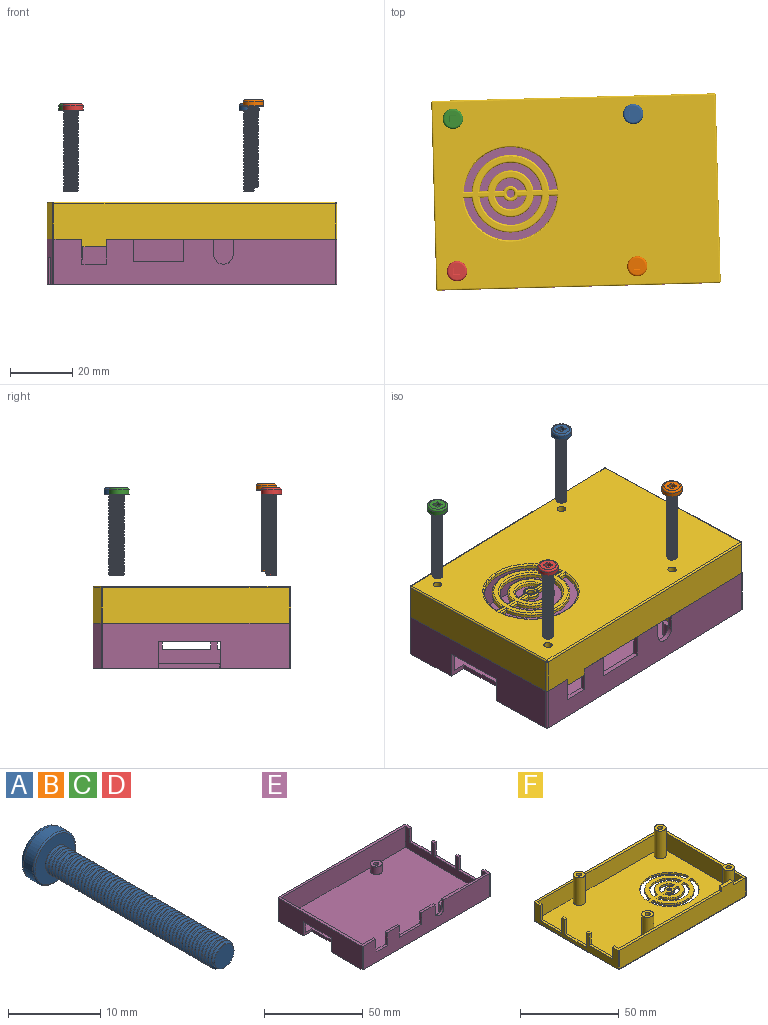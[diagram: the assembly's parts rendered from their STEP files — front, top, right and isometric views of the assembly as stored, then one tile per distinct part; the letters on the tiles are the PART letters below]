
ASSEMBLY  parts=6 mates=5
PART A: 21 faces, bbox 7.2x28.3x7.2 mm
  f0: plane 5.24x5.24mm, normal (0,1,0), area 16.8mm2, adj f4,f17,f18,f19,f20
  f1: plane 6.29x6.29mm, normal (0,-1,0), area 22mm2, adj f2,f5,f9,f10,f11
  f2: cylinder r=1.5mm len=26mm, axis (0,1,0), area 291.6mm2, adj f1,f6,f8,f9,f10,f11
  f3: cylinder r=3.25mm len=6.5mm, axis (0,1,0), area 28.7mm2, adj f4,f5
  f4: torus R=2.62mm, axis (0,-1,0), area 18.7mm2, adj f0,f3
  f5: torus R=3.08mm, axis (0,-1,0), area 5.3mm2, adj f1,f3
  f6: plane 3x3mm, normal (0,-1,0), area 7.1mm2, adj f2,f7
  f7: cylinder r=1.5mm len=0.03mm, axis (0,1,0), area 0mm2, adj f6,f8,f11
  f8: plane 0.3x0.26mm, normal (0,0,-1), area 0mm2, adj f2,f7,f10,f11
  f9: plane 0x0mm, normal (0,0,1), area 0mm2, adj f1,f2,f11
  f10: bspline ~26.07x4.07mm, area 159.4mm2, adj f1,f2,f8,f11
  f11: bspline ~26.15x4.07mm, area 158.7mm2, adj f1,f2,f7,f8,f9,f10
  f12: plane 2x1.1mm, normal (0,0,1), area 2.2mm2, adj f13,f15,f16,f17
  f13: plane 2x1.1mm, normal (1,0,0), area 2.2mm2, adj f12,f14,f16,f18
  f14: plane 2x1.1mm, normal (0,0,-1), area 2.2mm2, adj f13,f15,f16,f20
  f15: plane 2x1.1mm, normal (-1,0,0), area 2.2mm2, adj f12,f14,f16,f19
  f16: plane 2x2mm, normal (0,1,0), area 4mm2, adj f12,f13,f14,f15
  f17: cylinder r=0.1mm len=2.2mm, axis (-1,0,0), area 0.3mm2, adj f0,f12,f18,f19
  f18: cylinder r=0.1mm len=2.2mm, axis (0,0,1), area 0.3mm2, adj f0,f13,f17,f20
  f19: cylinder r=0.1mm len=2.2mm, axis (0,0,-1), area 0.3mm2, adj f0,f15,f17,f20
  f20: cylinder r=0.1mm len=2.2mm, axis (1,0,0), area 0.3mm2, adj f0,f14,f18,f19
PART B: same geometry as A
PART C: same geometry as A
PART D: same geometry as A
PART E: 58 faces, bbox 91.5x61x14.5 mm
  f0: plane 2x1.5mm, normal (0,0,1), area 3mm2, adj f3,f4,f33,f35
  f1: plane 2x1.5mm, normal (0,0,1), area 3mm2, adj f3,f4,f29,f32
  f2: plane 91.5x61mm, normal (0,0,1), area 243mm2, adj f3,f4,f5,f7,f11,f12,f13,f15
  f3: plane 60x14.5mm, normal (1,0,0), area 473.3mm2, adj f0,f1,f2,f10,f14,f29,f30,f31
  f4: plane 58x13mm, normal (-1,0,0), area 357.3mm2, adj f0,f1,f2,f6,f10,f11,f15,f29
  f5: plane 58x13mm, normal (1,0,0), area 611.4mm2, adj f2,f6,f11,f15,f25,f26,f27
  f6: plane 88.5x58mm, normal (0,0,1), area 4934.8mm2, adj f4,f5,f11,f15,f25,f26,f28,f39
  f7: plane 90.5x14.5mm, normal (0,-1,0), area 1086.9mm2, adj f2,f8,f9,f10,f14,f16,f17,f18
  f8: plane 8.7x1.5mm, normal (0,0,1), area 13mm2, adj f7,f11,f19,f24
  f9: plane 9.7x1.5mm, normal (0,0,1), area 14.5mm2, adj f7,f11,f18,f21
  f10: plane 33.3x4.6mm, normal (0,0,1), area 54.5mm2, adj f3,f4,f7,f11,f17,f36,f55
  f11: plane 88.5x13mm, normal (0,1,0), area 925.2mm2, adj f2,f4,f5,f6,f8,f9,f10,f16
  f12: plane 60x14.5mm, normal (-1,0,0), area 697.7mm2, adj f2,f14,f25,f26,f27,f54,f57
  f13: plane 90.5x14.5mm, normal (0,1,0), area 1312.3mm2, adj f2,f14,f56,f57
  f14: plane 91.5x61mm, normal (0,0,-1), area 5466.4mm2, adj f3,f7,f12,f13,f25,f26,f28,f54
  f15: plane 88.5x13mm, normal (0,-1,0), area 1150.5mm2, adj f2,f4,f5,f6
  f16: cylinder r=3.15mm len=6.3mm, axis (0,-1,0), area 14.8mm2, adj f7,f11,f17,f18
  f17: plane 4.85x1.5mm, normal (-1,0,0), area 7.3mm2, adj f7,f10,f11,f16
  f18: plane 4.85x1.5mm, normal (1,0,0), area 7.3mm2, adj f7,f9,f11,f16
  f19: plane 7.2x1.5mm, normal (1,0,0), area 10.8mm2, adj f7,f8,f11,f20
  f20: plane 16x1.5mm, normal (0,0,1), area 24mm2, adj f7,f11,f19,f21
  f21: plane 7.2x1.5mm, normal (-1,0,0), area 10.8mm2, adj f7,f9,f11,f20
  f22: plane 8x1.5mm, normal (1,0,0), area 12mm2, adj f2,f7,f11,f23
  f23: plane 8x1.5mm, normal (0,0,1), area 12mm2, adj f7,f11,f22,f24
  f24: plane 8x1.5mm, normal (-1,0,0), area 12mm2, adj f7,f8,f11,f23
  f25: plane 8.7x5.8mm, normal (0,-1,0), area 19.5mm2, adj f5,f6,f12,f14,f27,f28
  f26: plane 8.7x5.8mm, normal (0,1,0), area 19.5mm2, adj f5,f6,f12,f14,f27,f28
  f27: plane 19.8x1.5mm, normal (0,0,-1), area 29.7mm2, adj f5,f12,f25,f26
  f28: plane 19.8x1.5mm, normal (-1,0,0), area 29.7mm2, adj f6,f14,f25,f26
  f29: plane 8.3x1.5mm, normal (0,1,0), area 12.5mm2, adj f1,f3,f4,f30
  f30: plane 15.6x1.5mm, normal (0,0,1), area 23.4mm2, adj f3,f4,f29,f31
  f31: plane 8.3x1.5mm, normal (0,-1,0), area 12.5mm2, adj f2,f3,f4,f30
  f32: plane 8.3x1.5mm, normal (0,-1,0), area 12.5mm2, adj f1,f3,f4,f34
  f33: plane 8.3x1.5mm, normal (0,1,0), area 12.5mm2, adj f0,f3,f4,f34
  f34: plane 15.6x1.5mm, normal (0,0,1), area 23.4mm2, adj f3,f4,f32,f33
  f35: plane 8.3x1.5mm, normal (0,-1,0), area 12.5mm2, adj f0,f3,f4,f37
  f36: plane 8.3x1.5mm, normal (0,1,0), area 12.5mm2, adj f3,f4,f10,f37
  f37: plane 16.6x1.5mm, normal (0,0,1), area 24.9mm2, adj f3,f4,f35,f36
  f38: cylinder r=1.32mm len=4.7mm, axis (0,0,-1), area 39.1mm2, adj f40,f41
  f39: cylinder r=3mm len=6mm, axis (0,0,-1), area 88.6mm2, adj f6,f40
  f40: plane 6x6mm, normal (0,0,1), area 22.8mm2, adj f38,f39
  f41: plane 2.65x2.65mm, normal (0,0,1), area 5.5mm2, adj f38
  f42: cylinder r=1.32mm len=4.7mm, axis (0,0,-1), area 39.1mm2, adj f44,f45
  f43: cylinder r=3mm len=6mm, axis (0,0,-1), area 88.6mm2, adj f6,f44
  f44: plane 6x6mm, normal (0,0,1), area 22.8mm2, adj f42,f43
  f45: plane 2.65x2.65mm, normal (0,0,1), area 5.5mm2, adj f42
  f46: cylinder r=1.32mm len=4.7mm, axis (0,0,-1), area 39.1mm2, adj f48,f49
  f47: cylinder r=3mm len=6mm, axis (0,0,-1), area 88.6mm2, adj f6,f48
  f48: plane 6x6mm, normal (0,0,1), area 22.8mm2, adj f46,f47
  f49: plane 2.65x2.65mm, normal (0,0,1), area 5.5mm2, adj f46
  f50: cylinder r=1.32mm len=4.7mm, axis (0,0,-1), area 39.1mm2, adj f52,f53
  f51: cylinder r=3mm len=6mm, axis (0,0,-1), area 88.6mm2, adj f6,f52
  f52: plane 6x6mm, normal (0,0,1), area 22.8mm2, adj f50,f51
  f53: plane 2.65x2.65mm, normal (0,0,1), area 5.5mm2, adj f50
  f54: cylinder r=0.5mm len=14.5mm, axis (0,0,-1), area 11.4mm2, adj f2,f7,f12,f14
  f55: cylinder r=0.5mm len=14.5mm, axis (0,0,1), area 11.4mm2, adj f3,f7,f10,f14
  f56: cylinder r=0.5mm len=14.5mm, axis (0,0,-1), area 11.4mm2, adj f2,f3,f13,f14
  f57: cylinder r=0.5mm len=14.5mm, axis (0,0,1), area 11.4mm2, adj f2,f12,f13,f14
PART F: 102 faces, bbox 91.5x61x18.6 mm
  f0: plane 90.5x60mm, normal (0,0,-1), area 4841.6mm2, adj f53,f56,f59,f62,f68,f69,f73,f74
  f1: plane 88.5x58mm, normal (0,0,1), area 4632.4mm2, adj f6,f11,f12,f13,f28,f29,f30,f31
  f2: plane 60x11.5mm, normal (-1,0,0), area 275.5mm2, adj f3,f4,f5,f10,f19,f20,f21,f22
  f3: plane 74x4.6mm, normal (0,0,1), area 115.6mm2, adj f2,f6,f9,f13,f15,f25,f65
  f4: plane 2x1.5mm, normal (0,0,1), area 3mm2, adj f2,f6,f24,f26
  f5: plane 2x1.5mm, normal (0,0,1), area 3mm2, adj f2,f6,f21,f22
  f6: plane 58x10.5mm, normal (1,0,0), area 194.5mm2, adj f1,f3,f4,f5,f10,f12,f13,f19
  f7: plane 60x11.5mm, normal (1,0,0), area 690mm2, adj f10,f70,f74,f76
  f8: plane 90.5x11.5mm, normal (0,1,0), area 1040.8mm2, adj f10,f67,f73,f76
  f9: plane 90.5x13.9mm, normal (0,-1,0), area 1059.9mm2, adj f3,f10,f15,f16,f17,f65,f69,f70
  f10: plane 91.5x61mm, normal (0,0,1), area 243mm2, adj f2,f6,f7,f8,f9,f11,f12,f13
  f11: plane 58x10.5mm, normal (-1,0,0), area 609mm2, adj f1,f10,f12,f13
  f12: plane 88.5x10.5mm, normal (0,-1,0), area 929.2mm2, adj f1,f6,f10,f11
  f13: plane 88.5x10.5mm, normal (0,1,0), area 929.2mm2, adj f1,f3,f6,f10,f11,f14
  f14: plane 8x0.5mm, normal (0,0,-1), area 4mm2, adj f13,f15,f16,f18
  f15: plane 2.4x2mm, normal (-1,0,0), area 4.8mm2, adj f3,f9,f14,f17,f18
  f16: plane 2.4x2mm, normal (1,0,0), area 4.8mm2, adj f9,f10,f14,f17,f18
  f17: plane 8x2mm, normal (0,0,1), area 16mm2, adj f9,f15,f16,f18
  f18: plane 8x2.4mm, normal (0,1,0), area 19.2mm2, adj f14,f15,f16,f17
  f19: plane 9.4x1.5mm, normal (0,-1,0), area 14.1mm2, adj f2,f6,f10,f20
  f20: plane 15.6x1.5mm, normal (0,0,1), area 23.4mm2, adj f2,f6,f19,f21
  f21: plane 9.4x1.5mm, normal (0,1,0), area 14.1mm2, adj f2,f5,f6,f20
  f22: plane 9.4x1.5mm, normal (0,-1,0), area 14.1mm2, adj f2,f5,f6,f23
  f23: plane 15.6x1.5mm, normal (0,0,1), area 23.4mm2, adj f2,f6,f22,f24
  f24: plane 9.4x1.5mm, normal (0,1,0), area 14.1mm2, adj f2,f4,f6,f23
  f25: plane 7.3x1.5mm, normal (0,1,0), area 11mm2, adj f2,f3,f6,f27
  f26: plane 7.3x1.5mm, normal (0,-1,0), area 11mm2, adj f2,f4,f6,f27
  f27: plane 16.6x1.5mm, normal (0,0,1), area 24.9mm2, adj f2,f6,f25,f26
  f28: plane 2.51x1mm, normal (0,-1,0), area 2.5mm2, adj f1,f29,f31,f99
  f29: cylinder r=15mm len=29.94mm, axis (0,0,-1), area 45.1mm2, adj f1,f28,f30,f101
  f30: plane 2.51x1mm, normal (0,-1,0), area 2.5mm2, adj f1,f29,f31,f100
  f31: cylinder r=12.5mm len=24.92mm, axis (0,0,-1), area 37.3mm2, adj f1,f28,f30,f98
  f32: plane 2.61x1mm, normal (0,1,0), area 2.6mm2, adj f1,f33,f35,f79
  f33: cylinder r=5mm len=9.8mm, axis (0,0,-1), area 13.7mm2, adj f1,f32,f34,f81
  f34: plane 2.61x1mm, normal (0,1,0), area 2.6mm2, adj f1,f33,f35,f80
  f35: cylinder r=2.5mm len=4.59mm, axis (0,0,-1), area 5.8mm2, adj f1,f32,f34,f78
  f36: plane 2.51x1mm, normal (0,1,0), area 2.5mm2, adj f1,f37,f39,f94
  f37: cylinder r=15mm len=29.94mm, axis (0,0,-1), area 45.1mm2, adj f1,f36,f38,f95
  f38: plane 2.51x1mm, normal (0,1,0), area 2.5mm2, adj f1,f37,f39,f97
  f39: cylinder r=12.5mm len=24.92mm, axis (0,0,-1), area 37.3mm2, adj f1,f36,f38,f96
  f40: cylinder r=7.5mm len=14.87mm, axis (0,0,-1), area 21.6mm2, adj f1,f41,f43,f92
  f41: plane 2.52x1mm, normal (0,-1,0), area 2.5mm2, adj f1,f40,f42,f93
  f42: cylinder r=10mm len=19.9mm, axis (0,0,-1), area 29.4mm2, adj f1,f41,f43,f91
  f43: plane 2.52x1mm, normal (0,-1,0), area 2.5mm2, adj f1,f40,f42,f90
  f44: plane 2.52x1mm, normal (0,1,0), area 2.5mm2, adj f1,f45,f47,f87
  f45: cylinder r=10mm len=19.9mm, axis (0,0,-1), area 29.4mm2, adj f1,f44,f46,f89
  f46: plane 2.52x1mm, normal (0,1,0), area 2.5mm2, adj f1,f45,f47,f88
  f47: cylinder r=7.5mm len=14.87mm, axis (0,0,-1), area 21.6mm2, adj f1,f44,f46,f86
  f48: plane 2.61x1mm, normal (0,-1,0), area 2.6mm2, adj f1,f49,f51,f83
  f49: cylinder r=5mm len=9.8mm, axis (0,0,-1), area 13.7mm2, adj f1,f48,f50,f85
  f50: plane 2.61x1mm, normal (0,-1,0), area 2.6mm2, adj f1,f49,f51,f84
  f51: cylinder r=2.5mm len=4.59mm, axis (0,0,-1), area 5.8mm2, adj f1,f48,f50,f82
  f52: cylinder r=1.25mm len=2.5mm, axis (0,0,-1), area 7.9mm2, adj f1,f77
  f53: cylinder r=1.32mm len=18.55mm, axis (0,0,-1), area 154.4mm2, adj f0,f55
  f54: cylinder r=3mm len=17.05mm, axis (0,0,-1), area 321.4mm2, adj f1,f55
  f55: plane 6x6mm, normal (0,0,1), area 22.8mm2, adj f53,f54
  f56: cylinder r=1.32mm len=18.55mm, axis (0,0,-1), area 154.4mm2, adj f0,f58
  f57: cylinder r=3mm len=17.05mm, axis (0,0,-1), area 321.4mm2, adj f1,f58
  f58: plane 6x6mm, normal (0,0,1), area 22.8mm2, adj f56,f57
  f59: cylinder r=1.32mm len=18.55mm, axis (0,0,-1), area 154.4mm2, adj f0,f61
  f60: cylinder r=3mm len=17.05mm, axis (0,0,-1), area 321.4mm2, adj f1,f61
  f61: plane 6x6mm, normal (0,0,1), area 22.8mm2, adj f59,f60
  f62: cylinder r=1.32mm len=18.55mm, axis (0,0,-1), area 154.4mm2, adj f0,f64
  f63: cylinder r=3mm len=17.05mm, axis (0,0,-1), area 321.4mm2, adj f1,f64
  f64: plane 6x6mm, normal (0,0,1), area 22.8mm2, adj f62,f63
  f65: cylinder r=0.5mm len=11.5mm, axis (0,0,-1), area 9mm2, adj f2,f3,f9,f66
  f66: sphere r=0.5mm, area 0.4mm2, adj f65,f68,f69
  f67: cylinder r=0.5mm len=11.5mm, axis (0,0,1), area 9mm2, adj f2,f8,f10,f71
  f68: cylinder r=0.5mm len=60mm, axis (0,-1,0), area 47.1mm2, adj f0,f2,f66,f71
  f69: cylinder r=0.5mm len=90.5mm, axis (1,0,0), area 71.1mm2, adj f0,f9,f66,f72
  f70: cylinder r=0.5mm len=11.5mm, axis (0,0,1), area 9mm2, adj f7,f9,f10,f72
  f71: sphere r=0.5mm, area 0.4mm2, adj f67,f68,f73
  f72: sphere r=0.5mm, area 0.4mm2, adj f69,f70,f74
  f73: cylinder r=0.5mm len=90.5mm, axis (-1,0,0), area 71.1mm2, adj f0,f8,f71,f75
  f74: cylinder r=0.5mm len=60mm, axis (0,1,0), area 47.1mm2, adj f0,f7,f72,f75
  f75: sphere r=0.5mm, area 0.4mm2, adj f73,f74,f76
  f76: cylinder r=0.5mm len=11.5mm, axis (0,0,-1), area 9mm2, adj f7,f8,f10,f75
  f77: torus R=1.75mm, axis (0,0,1), area 7.1mm2, adj f0,f52
  f78: torus R=2mm, axis (0,0,1), area 4.4mm2, adj f0,f35,f79,f80
  f79: cylinder r=0.5mm len=3.54mm, axis (-1,0,0), area 2.3mm2, adj f0,f32,f78,f81
  f80: cylinder r=0.5mm len=3.54mm, axis (-1,0,0), area 2.3mm2, adj f0,f34,f78,f81
  f81: torus R=5.5mm, axis (0,0,1), area 11.5mm2, adj f0,f33,f79,f80
  f82: torus R=2mm, axis (0,0,1), area 4.4mm2, adj f0,f51,f83,f84
  f83: cylinder r=0.5mm len=3.54mm, axis (1,0,0), area 2.3mm2, adj f0,f48,f82,f85
  f84: cylinder r=0.5mm len=3.54mm, axis (1,0,0), area 2.3mm2, adj f0,f50,f82,f85
  f85: torus R=5.5mm, axis (0,0,1), area 11.5mm2, adj f0,f49,f83,f84
  f86: torus R=7mm, axis (0,0,1), area 16.8mm2, adj f0,f47,f87,f88
  f87: cylinder r=0.5mm len=3.51mm, axis (-1,0,0), area 2.3mm2, adj f0,f44,f86,f89
  f88: cylinder r=0.5mm len=3.51mm, axis (-1,0,0), area 2.3mm2, adj f0,f46,f86,f89
  f89: torus R=10.5mm, axis (0,0,1), area 23.9mm2, adj f0,f45,f87,f88
  f90: cylinder r=0.5mm len=3.51mm, axis (1,0,0), area 2.3mm2, adj f0,f43,f91,f92
  f91: torus R=10.5mm, axis (0,0,1), area 23.9mm2, adj f0,f42,f90,f93
  f92: torus R=7mm, axis (0,0,1), area 16.8mm2, adj f0,f40,f90,f93
  f93: cylinder r=0.5mm len=3.51mm, axis (1,0,0), area 2.3mm2, adj f0,f41,f91,f92
  f94: cylinder r=0.5mm len=3.5mm, axis (-1,0,0), area 2.3mm2, adj f0,f36,f95,f96
  f95: torus R=15.5mm, axis (0,0,1), area 36.2mm2, adj f0,f37,f94,f97
  f96: torus R=12mm, axis (0,0,1), area 29.1mm2, adj f0,f39,f94,f97
  f97: cylinder r=0.5mm len=3.5mm, axis (-1,0,0), area 2.3mm2, adj f0,f38,f95,f96
  f98: torus R=12mm, axis (0,0,1), area 29.1mm2, adj f0,f31,f99,f100
  f99: cylinder r=0.5mm len=3.5mm, axis (1,0,0), area 2.3mm2, adj f0,f28,f98,f101
  f100: cylinder r=0.5mm len=3.5mm, axis (1,0,0), area 2.3mm2, adj f0,f30,f98,f101
  f101: torus R=15.5mm, axis (0,0,1), area 36.2mm2, adj f0,f29,f99,f100
PLACE A rot(axis=(1,0,0),90deg) t=(-87,11.02,52.7)mm
PLACE B rot(axis=(1,0,0),90deg) t=(-85.67,-37.97,54.08)mm
PLACE C rot(axis=(1,0,0),90deg) t=(-144.98,9.44,52.7)mm
PLACE D rot(axis=(1,0,0),90deg) t=(-143.65,-39.54,52.73)mm
PLACE E rot(axis=(0,0,1),1.6deg) t=(-105.37,-13.99,-5.36)mm
PLACE F rot(axis=(0.01,-1,0),180deg) t=(-105.37,-13.99,21.14)mm
MATE cylindrical F.f59 <-> A.f2  axis (0,0,1) through (-87,11.02,21.14)mm
MATE cylindrical C.f2 <-> F.f53  axis (0,0,-1) through (-144.98,9.44,24.5)mm
MATE cylindrical B.f2 <-> F.f62  axis (0,0,-1) through (-85.67,-37.97,25.88)mm
MATE cylindrical D.f2 <-> F.f56  axis (0,0,-1) through (-143.65,-39.54,24.53)mm
MATE fastened F.f67 <-> E.f56  axis (0,0,-1) through (-60.95,17.23,9.14)mm
